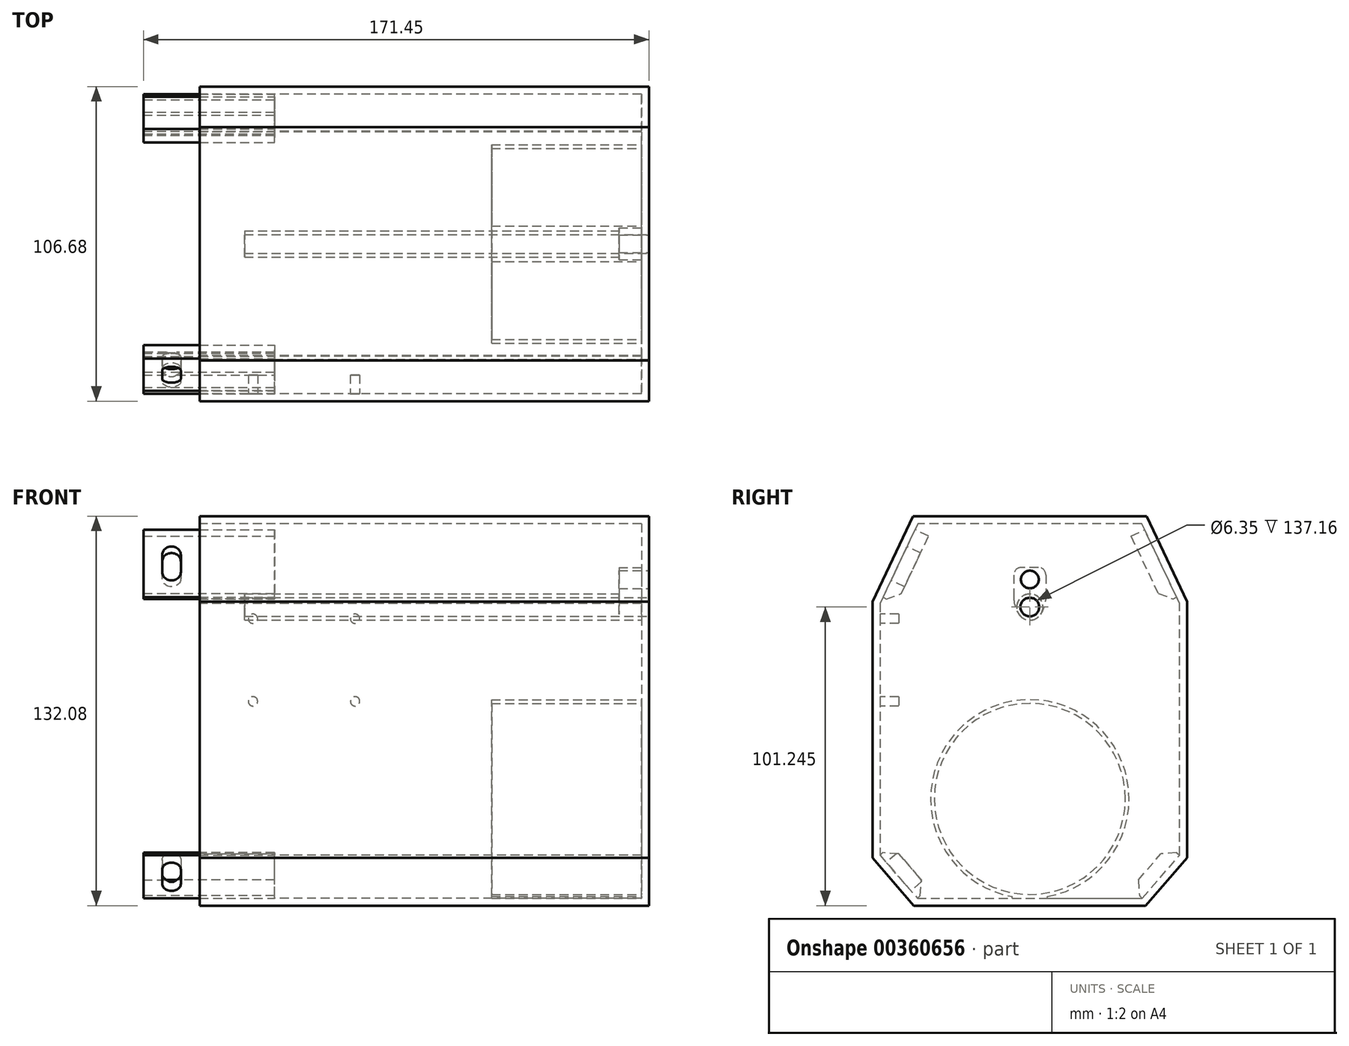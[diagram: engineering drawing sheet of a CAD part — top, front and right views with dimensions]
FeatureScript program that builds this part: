
annotation { "Feature Type Name" : "Feature", "Feature Type Description" : "" }
export const myFeature = defineFeature(function(context is Context, id is Id, definition is map)
    precondition{}
    {
        {
            var Q0;
            Q0=qCreatedBy(makeId("Right.planeOp"),FACE);
            var sketch = newSketch(context, id + "F0", { "sketchPlane" : qUnion([Q0])});
            skLineSegment(sketch, "E0", {"start": v(39.57, 69.02) * mm, "end": v(-39.57, 69.02) * mm});
            skLineSegment(sketch, "E1", {"start": v(-39.57, 69.02) * mm, "end": v(-53.34, 40) * mm});
            skLineSegment(sketch, "E2", {"start": v(-53.34, 40) * mm, "end": v(-53.34, -46.9) * mm});
            skLineSegment(sketch, "E3", {"start": v(-39.3, -63.06) * mm, "end": v(39.3, -63.06) * mm});
            skLineSegment(sketch, "E4", {"start": v(53.34, -46.9) * mm, "end": v(53.34, 40) * mm});
            skLineSegment(sketch, "E5", {"start": v(53.34, 40) * mm, "end": v(39.57, 69.02) * mm});
            skLineSegment(sketch, "E6", {"start": v(0, 69.02) * mm, "end": v(0, -63.06) * mm, "construction": true});
            skLineSegment(sketch, "E7", {"start": v(-53.34, -46.9) * mm, "end": v(-39.3, -63.06) * mm});
            skLineSegment(sketch, "E8", {"start": v(39.3, -63.06) * mm, "end": v(53.34, -46.9) * mm});
            skLineSegment(sketch, "E9.0", {"start": v(-50.8, 39.43) * mm, "end": v(-50.8, -45.94) * mm});
            skLineSegment(sketch, "E9.1", {"start": v(-37.96, 66.48) * mm, "end": v(-50.8, 39.43) * mm});
            skLineSegment(sketch, "E9.2", {"start": v(-50.8, -45.94) * mm, "end": v(-38.15, -60.52) * mm});
            skLineSegment(sketch, "E9.3", {"start": v(37.96, 66.48) * mm, "end": v(-37.96, 66.48) * mm});
            skLineSegment(sketch, "E9.4", {"start": v(-38.15, -60.52) * mm, "end": v(38.15, -60.52) * mm});
            skLineSegment(sketch, "E9.5", {"start": v(38.15, -60.52) * mm, "end": v(50.8, -45.94) * mm});
            skLineSegment(sketch, "E9.6", {"start": v(50.8, -45.94) * mm, "end": v(50.8, 39.43) * mm});
            skLineSegment(sketch, "E9.7", {"start": v(50.8, 39.43) * mm, "end": v(37.96, 66.48) * mm});
            skPoint(sketch, "E10", {"position": v(-50.8, 0) * mm});
            skSolve(sketch);
        }
        {
            var Q0;
            Q0 = qSketchRegion(id + "F0", true);
            extrude(context, id + "F1", {"entities" : qUnion([Q0]), "depth" : 152.4 * mm});
        }
        {
            var Q0;
            Q0=makeQuery(id+"F1.opExtrude","CAP_FACE",FACE,{"disambiguationData":[OSD([sQuery(id+"F0.wireOp",EDGE,"E0"),sQuery(id+"F0.wireOp",EDGE,"E1"),sQuery(id+"F0.wireOp",EDGE,"E2"),sQuery(id+"F0.wireOp",EDGE,"E3"),sQuery(id+"F0.wireOp",EDGE,"E4"),sQuery(id+"F0.wireOp",EDGE,"E5"),sQuery(id+"F0.wireOp",EDGE,"E7"),sQuery(id+"F0.wireOp",EDGE,"E8"),sQuery(id+"F0.wireOp",EDGE,"E9.0"),sQuery(id+"F0.wireOp",EDGE,"E9.1"),sQuery(id+"F0.wireOp",EDGE,"E9.2"),sQuery(id+"F0.wireOp",EDGE,"E9.3"),sQuery(id+"F0.wireOp",EDGE,"E9.4"),sQuery(id+"F0.wireOp",EDGE,"E9.5"),sQuery(id+"F0.wireOp",EDGE,"E9.6"),sQuery(id+"F0.wireOp",EDGE,"E9.7")])],"isStart":false});
            var sketch = newSketch(context, id + "F2", { "sketchPlane" : qUnion([Q0])});
            skLineSegment(sketch, "E11.0", {"start": v(-39.57, 69.02) * mm, "end": v(-53.34, 40) * mm});
            skLineSegment(sketch, "E12.0", {"start": v(-53.34, 40) * mm, "end": v(-53.34, -46.9) * mm});
            skLineSegment(sketch, "E13.0", {"start": v(-53.34, -46.9) * mm, "end": v(-39.3, -63.06) * mm});
            skLineSegment(sketch, "E14.0", {"start": v(-39.3, -63.06) * mm, "end": v(39.3, -63.06) * mm});
            skLineSegment(sketch, "E15.0", {"start": v(39.3, -63.06) * mm, "end": v(53.34, -46.9) * mm});
            skLineSegment(sketch, "E16.0", {"start": v(53.34, -46.9) * mm, "end": v(53.34, 40) * mm});
            skLineSegment(sketch, "E17.0", {"start": v(53.34, 40) * mm, "end": v(39.57, 69.02) * mm});
            skLineSegment(sketch, "E18.0", {"start": v(39.57, 69.02) * mm, "end": v(-39.57, 69.02) * mm});
            skSolve(sketch);
        }
        {
            var Q0;
            Q0 = qSketchRegion(id + "F2", true);
            extrude(context, id + "F3", {"entities" : qUnion([Q0]), "operationType" : NewBodyOperationType.ADD, "oppositeDirection" : true, "depth" : 2.54 * mm});
        }
        {
            var Q0;
            Q0=makeQuery(id+"F3.opExtrude","CAP_FACE",FACE,{"disambiguationData":[OSD([sQuery(id+"F2.wireOp",EDGE,"E11.0"),sQuery(id+"F2.wireOp",EDGE,"E12.0"),sQuery(id+"F2.wireOp",EDGE,"E13.0"),sQuery(id+"F2.wireOp",EDGE,"E14.0"),sQuery(id+"F2.wireOp",EDGE,"E15.0"),sQuery(id+"F2.wireOp",EDGE,"E16.0"),sQuery(id+"F2.wireOp",EDGE,"E17.0"),sQuery(id+"F2.wireOp",EDGE,"E18.0")])],"isStart":false});
            var sketch = newSketch(context, id + "F4", { "sketchPlane" : qUnion([Q0])});
            skArc(sketch, "E19", {"start": v(5.97, -59.99) * mm, "mid": v(0, 6.79) * mm, "end": v(-5.97, -59.99) * mm});
            skCircle(sketch, "E20", {"center": v(0, -26.87) * mm, "radius": 32.39 * mm});
            skLineSegment(sketch, "E21", {"start": v(-5.97, -60.52) * mm, "end": v(-5.97, -59.99) * mm});
            skLineSegment(sketch, "E22.MirrorCS", {"start": v(5.97, -60.52) * mm, "end": v(5.97, -59.99) * mm});
            skLineSegment(sketch, "E23", {"start": v(-5.97, -60.52) * mm, "end": v(5.97, -60.52) * mm});
            skSolve(sketch);
        }
        {
            var Q0;
            Q0 = qSketchRegion(id + "F4", true);
            extrude(context, id + "F5", {"entities" : qUnion([Q0]), "operationType" : NewBodyOperationType.ADD, "depth" : 50.8 * mm});
        }
        {
            var Q0;
            Q0=makeQuery(id+"F5.boolean.opBoolean","SPLIT",FACE,{"disambiguationData":[TD([makeQuery(id+"F1.opExtrude","SWEPT_FACE",FACE,{"disambiguationData":[OSD([sQuery(id+"F0.wireOp",EDGE,"E9.0")])]})])],"derivedFrom":makeQuery(id+"F3.opExtrude","CAP_FACE",FACE,{"disambiguationData":[OSD([sQuery(id+"F2.wireOp",EDGE,"E11.0"),sQuery(id+"F2.wireOp",EDGE,"E12.0"),sQuery(id+"F2.wireOp",EDGE,"E13.0"),sQuery(id+"F2.wireOp",EDGE,"E14.0"),sQuery(id+"F2.wireOp",EDGE,"E15.0"),sQuery(id+"F2.wireOp",EDGE,"E16.0"),sQuery(id+"F2.wireOp",EDGE,"E17.0"),sQuery(id+"F2.wireOp",EDGE,"E18.0")])],"isStart":false})});
            var sketch = newSketch(context, id + "F6", { "sketchPlane" : qUnion([Q0])});
            skCircle(sketch, "E24", {"center": v(0, 47.53) * mm, "radius": 3 * mm});
            skCircle(sketch, "E25", {"center": v(0, 38.18) * mm, "radius": 4.45 * mm});
            skLineSegment(sketch, "E26.bottom", {"start": v(-2.9, 51.62) * mm, "end": v(2.9, 51.62) * mm});
            skLineSegment(sketch, "E26.left", {"start": v(-5.44, 49.08) * mm, "end": v(-5.44, 41.46) * mm});
            skLineSegment(sketch, "E26.right", {"start": v(5.44, 49.08) * mm, "end": v(5.44, 41.46) * mm});
            skPoint(sketch, "E27", {"position": v(0, 51.62) * mm});
            skPoint(sketch, "E28.visualSharp", {"position": v(-5.44, 51.62) * mm});
            skArc(sketch, "E28.filletArc", {"start": v(-2.9, 51.62) * mm, "mid": v(-4.7, 50.88) * mm, "end": v(-5.44, 49.08) * mm});
            skPoint(sketch, "E29.visualSharp", {"position": v(5.44, 51.62) * mm});
            skArc(sketch, "E29.filletArc", {"start": v(5.44, 49.08) * mm, "mid": v(4.7, 50.88) * mm, "end": v(2.9, 51.62) * mm});
            skPoint(sketch, "E30.visualSharp", {"position": v(5.44, 32.75) * mm});
            skPoint(sketch, "E31.visualSharp", {"position": v(-5.44, 32.75) * mm});
            skCircle(sketch, "E32", {"center": v(0, 38.18) * mm, "radius": 3.18 * mm});
            skArc(sketch, "E33", {"start": v(-5.44, 41.46) * mm, "mid": v(-5, 38.45) * mm, "end": v(-3.7, 35.7) * mm});
            skArc(sketch, "E34", {"start": v(3.7, 35.7) * mm, "mid": v(5, 38.45) * mm, "end": v(5.44, 41.46) * mm});
            skSolve(sketch);
        }
        {
            var Q0;
            Q0 = qSketchRegion(id + "F6", true);
            extrude(context, id + "F7", {"entities" : qUnion([Q0]), "operationType" : NewBodyOperationType.ADD, "depth" : 7.62 * mm});
        }
        {
            var Q0;
            Q0=makeQuery(id+"F7.opExtrude","CAP_FACE",FACE,{"disambiguationData":[OSD([sQuery(id+"F6.wireOp",EDGE,"E24"),sQuery(id+"F6.wireOp",EDGE,"E25"),sQuery(id+"F6.wireOp",EDGE,"E26.bottom"),sQuery(id+"F6.wireOp",EDGE,"E26.top"),sQuery(id+"F6.wireOp",EDGE,"E26.left"),sQuery(id+"F6.wireOp",EDGE,"E26.right"),sQuery(id+"F6.wireOp",EDGE,"E28.filletArc"),sQuery(id+"F6.wireOp",EDGE,"E29.filletArc"),sQuery(id+"F6.wireOp",EDGE,"E30.filletArc"),sQuery(id+"F6.wireOp",EDGE,"E31.filletArc")])],"isStart":false});
            var sketch = newSketch(context, id + "F8", { "sketchPlane" : qUnion([Q0])});
            skCircle(sketch, "E35", {"center": v(0, 38.18) * mm, "radius": 4.45 * mm});
            skCircle(sketch, "E36", {"center": v(0, 38.18) * mm, "radius": 3.18 * mm});
            skSolve(sketch);
        }
        {
            var Q0;
            Q0 = qSketchRegion(id + "F8", true);
            extrude(context, id + "F9", {"entities" : qUnion([Q0]), "operationType" : NewBodyOperationType.ADD, "depth" : 127 * mm});
        }
        {
            var Q0;
            Q0=makeQuery(id+"F7.boolean.opBoolean","SPLIT",FACE,{"disambiguationData":[TD([makeQuery(id+"F7.opExtrude","SWEPT_FACE",FACE,{"disambiguationData":[OSD([sQuery(id+"F6.wireOp",EDGE,"E24")])]})])],"derivedFrom":makeQuery(id+"F5.boolean.opBoolean","SPLIT",FACE,{"disambiguationData":[TD([makeQuery(id+"F1.opExtrude","SWEPT_FACE",FACE,{"disambiguationData":[OSD([sQuery(id+"F0.wireOp",EDGE,"E9.0")])]})])],"derivedFrom":makeQuery(id+"F3.opExtrude","CAP_FACE",FACE,{"disambiguationData":[OSD([sQuery(id+"F2.wireOp",EDGE,"E11.0"),sQuery(id+"F2.wireOp",EDGE,"E12.0"),sQuery(id+"F2.wireOp",EDGE,"E13.0"),sQuery(id+"F2.wireOp",EDGE,"E14.0"),sQuery(id+"F2.wireOp",EDGE,"E15.0"),sQuery(id+"F2.wireOp",EDGE,"E16.0"),sQuery(id+"F2.wireOp",EDGE,"E17.0"),sQuery(id+"F2.wireOp",EDGE,"E18.0")])],"isStart":false})})});
            var Q1;
            Q1=makeQuery(id+"F7.boolean.opBoolean","SPLIT",FACE,{"disambiguationData":[TD([makeQuery(id+"F7.opExtrude","SWEPT_FACE",FACE,{"disambiguationData":[OSD([sQuery(id+"F6.wireOp",EDGE,"E32")])]})])],"derivedFrom":makeQuery(id+"F5.boolean.opBoolean","SPLIT",FACE,{"disambiguationData":[TD([makeQuery(id+"F1.opExtrude","SWEPT_FACE",FACE,{"disambiguationData":[OSD([sQuery(id+"F0.wireOp",EDGE,"E9.0")])]})])],"derivedFrom":makeQuery(id+"F3.opExtrude","CAP_FACE",FACE,{"disambiguationData":[OSD([sQuery(id+"F2.wireOp",EDGE,"E11.0"),sQuery(id+"F2.wireOp",EDGE,"E12.0"),sQuery(id+"F2.wireOp",EDGE,"E13.0"),sQuery(id+"F2.wireOp",EDGE,"E14.0"),sQuery(id+"F2.wireOp",EDGE,"E15.0"),sQuery(id+"F2.wireOp",EDGE,"E16.0"),sQuery(id+"F2.wireOp",EDGE,"E17.0"),sQuery(id+"F2.wireOp",EDGE,"E18.0")])],"isStart":false})})});
            extrude(context, id + "F10", {"entities" : qUnion([Q0, Q1]), "operationType" : NewBodyOperationType.REMOVE, "oppositeDirection" : true, "depth" : 25.4 * mm});
        }
        {
            var Q0;
            Q0=makeQuery(id+"F1.opExtrude","SWEPT_FACE",FACE,{"disambiguationData":[OSD([sQuery(id+"F0.wireOp",EDGE,"E9.0")])]});
            var sketch = newSketch(context, id + "F11", { "sketchPlane" : qUnion([Q0])});
            skLineSegment(sketch, "E37.bottom", {"start": v(-52.73, 34.23) * mm, "end": v(-18.08, 34.23) * mm, "construction": true});
            skLineSegment(sketch, "E37.top", {"start": v(-52.73, 6.21) * mm, "end": v(-18.08, 6.21) * mm, "construction": true});
            skLineSegment(sketch, "E37.left", {"start": v(-52.73, 34.23) * mm, "end": v(-52.73, 6.21) * mm, "construction": true});
            skLineSegment(sketch, "E37.right", {"start": v(-18.08, 34.23) * mm, "end": v(-18.08, 6.21) * mm, "construction": true});
            skCircle(sketch, "E38", {"center": v(-52.73, 34.23) * mm, "radius": 1.59 * mm});
            skCircle(sketch, "E39", {"center": v(-18.08, 34.23) * mm, "radius": 1.59 * mm});
            skCircle(sketch, "E40", {"center": v(-52.73, 6.21) * mm, "radius": 1.59 * mm});
            skCircle(sketch, "E41", {"center": v(-18.08, 6.21) * mm, "radius": 1.59 * mm});
            skSolve(sketch);
        }
        {
            var Q0;
            Q0 = qSketchRegion(id + "F11", true);
            extrude(context, id + "F12", {"entities" : qUnion([Q0]), "operationType" : NewBodyOperationType.ADD, "depth" : 6.35 * mm});
        }
        {
            var Q0;
            Q0=makeQuery(id+"F1.opExtrude","CAP_FACE",FACE,{"disambiguationData":[OSD([sQuery(id+"F0.wireOp",EDGE,"E0"),sQuery(id+"F0.wireOp",EDGE,"E1"),sQuery(id+"F0.wireOp",EDGE,"E2"),sQuery(id+"F0.wireOp",EDGE,"E3"),sQuery(id+"F0.wireOp",EDGE,"E4"),sQuery(id+"F0.wireOp",EDGE,"E5"),sQuery(id+"F0.wireOp",EDGE,"E7"),sQuery(id+"F0.wireOp",EDGE,"E8"),sQuery(id+"F0.wireOp",EDGE,"E9.0"),sQuery(id+"F0.wireOp",EDGE,"E9.1"),sQuery(id+"F0.wireOp",EDGE,"E9.2"),sQuery(id+"F0.wireOp",EDGE,"E9.3"),sQuery(id+"F0.wireOp",EDGE,"E9.4"),sQuery(id+"F0.wireOp",EDGE,"E9.5"),sQuery(id+"F0.wireOp",EDGE,"E9.6"),sQuery(id+"F0.wireOp",EDGE,"E9.7")])],"isStart":true});
            var sketch = newSketch(context, id + "F13", { "sketchPlane" : qUnion([Q0])});
            skLineSegment(sketch, "E42", {"start": v(-38.94, 64.43) * mm, "end": v(-49.83, 41.48) * mm});
            skLineSegment(sketch, "E43", {"start": v(-49.83, 41.48) * mm, "end": v(-45.24, 39.3) * mm});
            skLineSegment(sketch, "E44", {"start": v(-45.24, 39.3) * mm, "end": v(-34.35, 62.25) * mm});
            skLineSegment(sketch, "E45", {"start": v(-34.35, 62.25) * mm, "end": v(-38.94, 64.43) * mm});
            skPoint(sketch, "E46", {"position": v(-44.38, 52.96) * mm});
            skPoint(sketch, "E47", {"position": v(-44.48, -53.23) * mm});
            skLineSegment(sketch, "E48", {"start": v(-50.8, -45.94) * mm, "end": v(-38.15, -60.52) * mm});
            skLineSegment(sketch, "E49", {"start": v(-38.15, -60.52) * mm, "end": v(-34.31, -57.2) * mm});
            skLineSegment(sketch, "E50", {"start": v(-34.31, -57.2) * mm, "end": v(-46.96, -42.61) * mm});
            skLineSegment(sketch, "E51", {"start": v(-46.96, -42.61) * mm, "end": v(-50.8, -45.94) * mm});
            skLineSegment(sketch, "E52", {"start": v(0, 60.5) * mm, "end": v(0, -29.03) * mm, "construction": true});
            skLineSegment(sketch, "E53.MirrorCS", {"start": v(49.83, 41.48) * mm, "end": v(45.24, 39.3) * mm});
            skLineSegment(sketch, "E54.MirrorCS", {"start": v(46.96, -42.61) * mm, "end": v(50.8, -45.94) * mm});
            skLineSegment(sketch, "E55.MirrorCS", {"start": v(34.35, 62.25) * mm, "end": v(38.94, 64.43) * mm});
            skLineSegment(sketch, "E56.MirrorCS", {"start": v(38.15, -60.52) * mm, "end": v(34.31, -57.2) * mm});
            skLineSegment(sketch, "E57.MirrorCS", {"start": v(34.31, -57.2) * mm, "end": v(46.96, -42.61) * mm});
            skLineSegment(sketch, "E58.MirrorCS", {"start": v(50.8, -45.94) * mm, "end": v(38.15, -60.52) * mm});
            skPoint(sketch, "E59.MirrorP", {"position": v(44.48, -53.23) * mm});
            skPoint(sketch, "E60.MirrorP", {"position": v(44.38, 52.96) * mm});
            skLineSegment(sketch, "E61.MirrorCS", {"start": v(38.94, 64.43) * mm, "end": v(49.83, 41.48) * mm});
            skLineSegment(sketch, "E62.MirrorCS", {"start": v(45.24, 39.3) * mm, "end": v(34.35, 62.25) * mm});
            skSolve(sketch);
        }
        {
            var Q0;
            Q0 = qSketchRegion(id + "F13", true);
            extrude(context, id + "F14", {"entities" : qUnion([Q0]), "operationType" : NewBodyOperationType.ADD, "depth" : 19.05 * mm, "hasSecondDirection" : true, "secondDirectionOppositeDirection" : true, "secondDirectionDepth" : 25.4 * mm});
        }
        {
            var Q0;
            Q0=makeQuery(id+"F14.opExtrude","SWEPT_FACE",FACE,{"disambiguationData":[OSD([sQuery(id+"F13.wireOp",EDGE,"E61.MirrorCS")])]});
            var sketch = newSketch(context, id + "F15", { "sketchPlane" : qUnion([Q0])});
            skLineSegment(sketch, "E63", {"start": v(-19.05, 28.81) * mm, "end": v(0, 28.81) * mm, "construction": true});
            skLineSegment(sketch, "E64", {"start": v(-9.52, 16.11) * mm, "end": v(-9.52, 41.51) * mm, "construction": true});
            skArc(sketch, "E65", {"start": v(-6.35, 31.99) * mm, "mid": v(-9.53, 35.16) * mm, "end": v(-12.7, 31.99) * mm});
            skArc(sketch, "E66", {"start": v(-12.7, 25.64) * mm, "mid": v(-9.53, 22.46) * mm, "end": v(-6.35, 25.64) * mm});
            skLineSegment(sketch, "E67", {"start": v(-12.7, 31.99) * mm, "end": v(-12.7, 25.64) * mm});
            skLineSegment(sketch, "E68", {"start": v(-6.35, 25.64) * mm, "end": v(-6.35, 31.99) * mm});
            skLineSegment(sketch, "E69", {"start": v(-9.52, 31.99) * mm, "end": v(-9.52, 25.64) * mm});
            skPoint(sketch, "E70", {"position": v(-9.53, 28.81) * mm});
            skSolve(sketch);
        }
        {
            var Q0;
            Q0 = qSketchRegion(id + "F15", true);
            extrude(context, id + "F16", {"entities" : qUnion([Q0]), "operationType" : NewBodyOperationType.REMOVE, "oppositeDirection" : true, "depth" : 25.4 * mm});
        }
        {
            var Q0;
            Q0=makeQuery(id+"F14.opExtrude","SWEPT_FACE",FACE,{"disambiguationData":[OSD([sQuery(id+"F13.wireOp",EDGE,"E58.MirrorCS")])]});
            var sketch = newSketch(context, id + "F17", { "sketchPlane" : qUnion([Q0])});
            skLineSegment(sketch, "E71", {"start": v(-9.53, -1.41) * mm, "end": v(-9.53, -20.71) * mm, "construction": true});
            skLineSegment(sketch, "E72", {"start": v(-19.05, -11.06) * mm, "end": v(0, -11.06) * mm, "construction": true});
            skPoint(sketch, "E73", {"position": v(-9.53, -11.06) * mm});
            skArc(sketch, "E74", {"start": v(-6.35, -7.89) * mm, "mid": v(-9.53, -4.71) * mm, "end": v(-12.7, -7.89) * mm});
            skArc(sketch, "E75", {"start": v(-12.7, -14.24) * mm, "mid": v(-9.52, -17.41) * mm, "end": v(-6.35, -14.24) * mm});
            skLineSegment(sketch, "E76", {"start": v(-12.7, -7.89) * mm, "end": v(-12.7, -14.24) * mm});
            skLineSegment(sketch, "E77", {"start": v(-6.35, -14.24) * mm, "end": v(-6.35, -7.89) * mm});
            skLineSegment(sketch, "E78", {"start": v(-9.53, -7.89) * mm, "end": v(-9.53, -14.24) * mm});
            skSolve(sketch);
        }
        {
            var Q0;
            Q0 = qSketchRegion(id + "F17", true);
            extrude(context, id + "F18", {"entities" : qUnion([Q0]), "operationType" : NewBodyOperationType.REMOVE, "oppositeDirection" : true, "depth" : 25.4 * mm});
        }
        {
            var Q0;
            Q0=makeQuery(id+"F14.opExtrude","SWEPT_EDGE",EDGE,{"disambiguationData":[OSD([sQuery(id+"F13.wireOp",EDGE,"E53.MirrorCS"),sQuery(id+"F13.wireOp",EDGE,"E62.MirrorCS")])]});
            var Q1;
            Q1=makeQuery(id+"F14.opExtrude","SWEPT_EDGE",EDGE,{"disambiguationData":[OSD([sQuery(id+"F13.wireOp",EDGE,"E43"),sQuery(id+"F13.wireOp",EDGE,"E44")])]});
            var Q2;
            Q2=makeQuery(id+"F14.opExtrude","SWEPT_EDGE",EDGE,{"disambiguationData":[OSD([sQuery(id+"F13.wireOp",EDGE,"E50"),sQuery(id+"F13.wireOp",EDGE,"E51")])]});
            var Q3;
            Q3=makeQuery(id+"F14.opExtrude","SWEPT_EDGE",EDGE,{"disambiguationData":[OSD([sQuery(id+"F13.wireOp",EDGE,"E49"),sQuery(id+"F13.wireOp",EDGE,"E50")])]});
            var Q4;
            Q4=makeQuery(id+"F14.opExtrude","SWEPT_EDGE",EDGE,{"disambiguationData":[OSD([sQuery(id+"F13.wireOp",EDGE,"E54.MirrorCS"),sQuery(id+"F13.wireOp",EDGE,"E57.MirrorCS")])]});
            var Q5;
            Q5=makeQuery(id+"F14.opExtrude","SWEPT_EDGE",EDGE,{"disambiguationData":[OSD([sQuery(id+"F13.wireOp",EDGE,"E56.MirrorCS"),sQuery(id+"F13.wireOp",EDGE,"E57.MirrorCS")])]});
            chamfer(context, id + "F19", {"entities" : qUnion([Q0, Q1, Q2, Q3, Q4, Q5]), "width" : 3.8 * mm, "tangentPropagation" : true});
        }
    });
